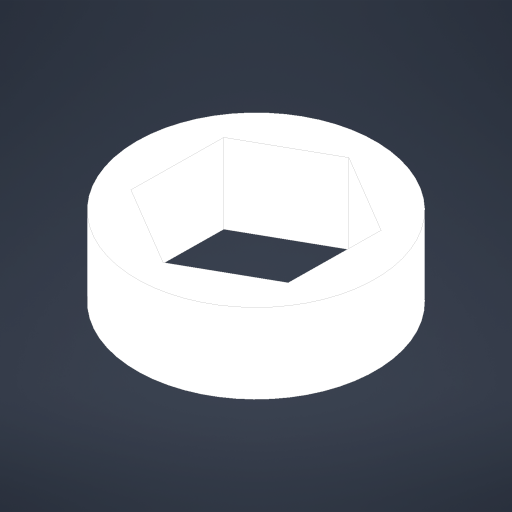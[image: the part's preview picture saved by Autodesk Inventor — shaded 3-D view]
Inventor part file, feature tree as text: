
AUTODESK INVENTOR PART (.ipt)
format: ipt  version: 2024.3 (Build 283343000, 343)  size: 158,720 bytes
history: native  units: in
note: dims shown in document units (in); Inventor stores cm internally (conversion verified against a paired STEP export)
features: extrude x1, sketch x1
ambient origin geometry x8: Origin, YZ Plane, XZ Plane, XY Plane, X Axis, Y Axis, Z Axis, Center Point
bodies: Solid1 (feature_tree)
feature tree (2):
  extrude  "Extrusion1"  Depth=0.5in
  sketch  "Sketch1"  dims[d0=0.75in d1=0.5in d2=0.25in d3=0.0in]
